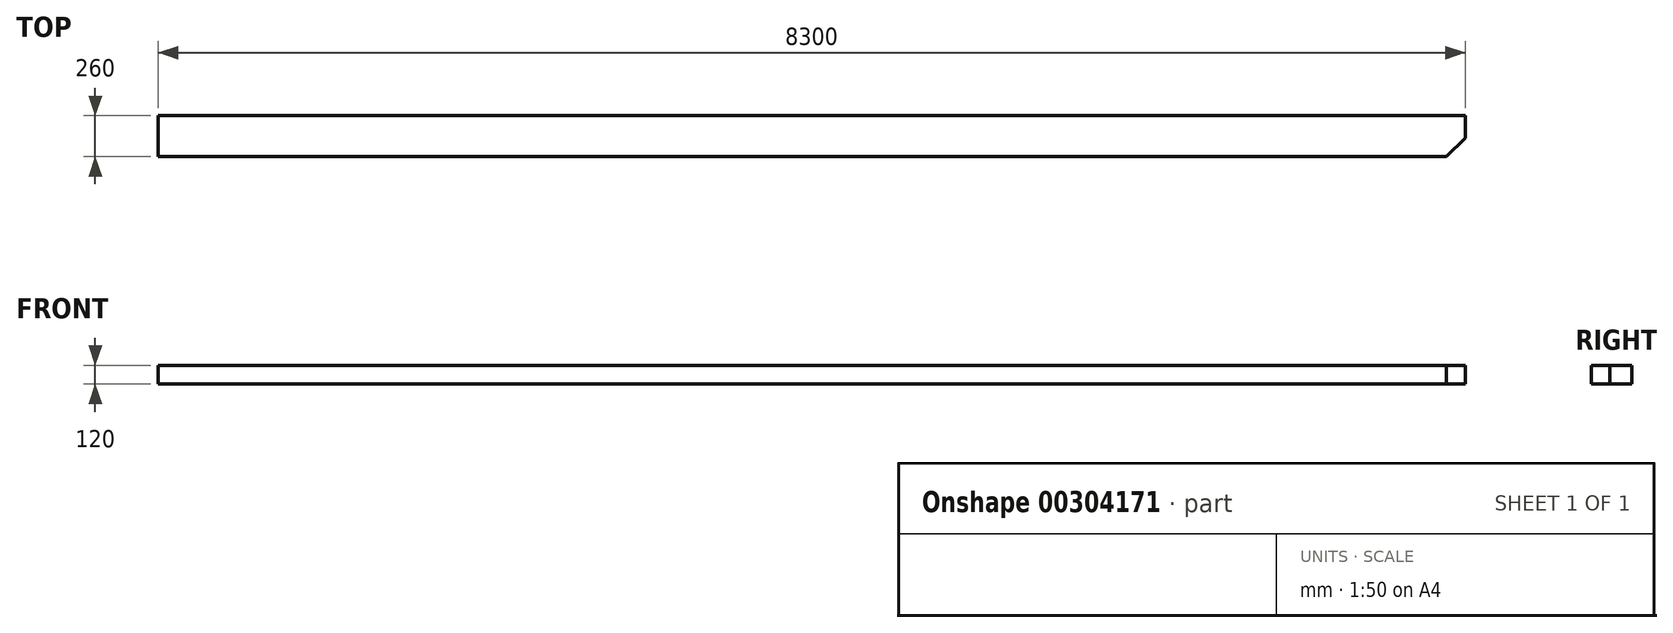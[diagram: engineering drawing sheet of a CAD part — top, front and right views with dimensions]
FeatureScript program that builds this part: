
annotation { "Feature Type Name" : "Feature", "Feature Type Description" : "" }
export const myFeature = defineFeature(function(context is Context, id is Id, definition is map)
    precondition{}
    {
        {
            var Q0;
            Q0=qCreatedBy(makeId("Top.planeOp"),FACE);
            var sketch = newSketch(context, id + "F0", { "sketchPlane" : qUnion([Q0])});
            skLineSegment(sketch, "E0.bottom", {"start": v(-4147.7, -80.85) * mm, "end": v(4152.3, -80.85) * mm});
            skLineSegment(sketch, "E0.top", {"start": v(-4147.7, -340.85) * mm, "end": v(4152.3, -340.85) * mm});
            skLineSegment(sketch, "E0.left", {"start": v(-4147.7, -80.85) * mm, "end": v(-4147.7, -340.85) * mm});
            skLineSegment(sketch, "E0.right", {"start": v(4152.3, -80.85) * mm, "end": v(4152.3, -340.85) * mm});
            skSolve(sketch);
        }
        {
            var Q0;
            Q0=makeQuery(id+"F0.imprint","IMPRINT",FACE,{"disambiguationData":[TD([[makeQuery(id+"F0.imprint","IMPRINT",EDGE,{"derivedFrom":sQuery(id+"F0.wireOp",EDGE,"E0.bottom")}),-1.0]])]});
            extrude(context, id + "F1", {"entities" : qUnion([Q0]), "depth" : 120 * mm});
        }
        {
            var Q0;
            Q0=makeQuery(id+"F1.opExtrude","SWEPT_EDGE",EDGE,{"disambiguationData":[OSD([sQuery(id+"F0.wireOp",EDGE,"E0.top"),sQuery(id+"F0.wireOp",EDGE,"E0.right")])]});
            chamfer(context, id + "F2", {"entities" : qUnion([Q0]), "chamferType" : ChamferType.TWO_OFFSETS, "width1" : 120 * mm, "oppositeDirection" : false, "width2" : 120 * mm, "tangentPropagation" : true});
        }
    });
